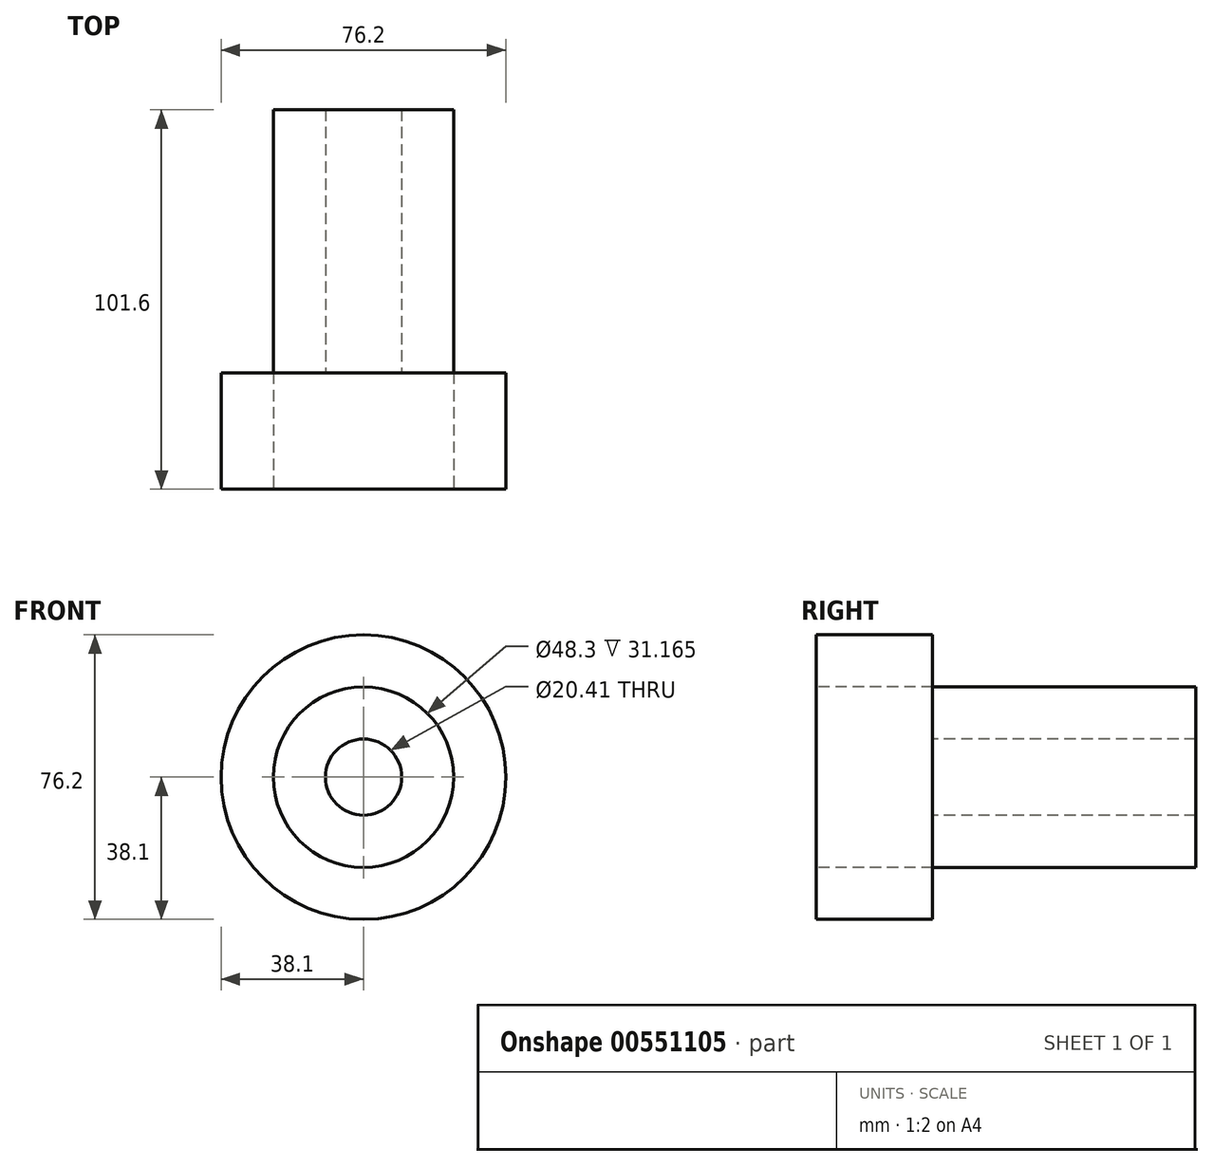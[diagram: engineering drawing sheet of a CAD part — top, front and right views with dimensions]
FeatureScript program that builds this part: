
annotation { "Feature Type Name" : "Feature", "Feature Type Description" : "" }
export const myFeature = defineFeature(function(context is Context, id is Id, definition is map)
    precondition{}
    {
        {
            var Q0;
            Q0=qCreatedBy(makeId("Right.planeOp"),FACE);
            var sketch = newSketch(context, id + "F0", { "sketchPlane" : qUnion([Q0])});
            skLineSegment(sketch, "E0", {"start": v(-31.17, 0) * mm, "end": v(70.43, 0) * mm, "construction": true});
            skLineSegment(sketch, "E1.bottom", {"start": v(-31.17, 38.1) * mm, "end": v(0, 38.1) * mm});
            skLineSegment(sketch, "E1.top", {"start": v(-31.17, 10.2) * mm, "end": v(0, 10.2) * mm});
            skLineSegment(sketch, "E1.left", {"start": v(-31.17, 38.1) * mm, "end": v(-31.17, 10.2) * mm});
            skLineSegment(sketch, "E1.right", {"start": v(0, 38.1) * mm, "end": v(0, 10.2) * mm});
            skLineSegment(sketch, "E2.bottom", {"start": v(-31.17, 24.15) * mm, "end": v(70.43, 24.15) * mm});
            skLineSegment(sketch, "E2.top", {"start": v(-31.17, 10.2) * mm, "end": v(70.43, 10.2) * mm});
            skLineSegment(sketch, "E2.left", {"start": v(-31.17, 24.15) * mm, "end": v(-31.17, 10.2) * mm});
            skLineSegment(sketch, "E2.right", {"start": v(70.43, 24.15) * mm, "end": v(70.43, 10.2) * mm});
            skLineSegment(sketch, "E3.MirrorCS", {"start": v(-31.17, -10.2) * mm, "end": v(0, -10.2) * mm});
            skLineSegment(sketch, "E4.MirrorCS", {"start": v(70.43, -24.15) * mm, "end": v(70.43, -10.2) * mm});
            skLineSegment(sketch, "E5.MirrorCS", {"start": v(-31.17, -24.15) * mm, "end": v(-31.17, -10.2) * mm});
            skLineSegment(sketch, "E6.MirrorCS", {"start": v(-31.17, -38.1) * mm, "end": v(0, -38.1) * mm});
            skLineSegment(sketch, "E7.MirrorCS", {"start": v(-31.17, -38.1) * mm, "end": v(-31.17, -10.2) * mm});
            skLineSegment(sketch, "E8.MirrorCS", {"start": v(0, -38.1) * mm, "end": v(0, -10.2) * mm});
            skLineSegment(sketch, "E9.MirrorCS", {"start": v(-31.17, -24.15) * mm, "end": v(70.43, -24.15) * mm});
            skLineSegment(sketch, "E10.MirrorCS", {"start": v(-31.17, -10.2) * mm, "end": v(70.43, -10.2) * mm});
            skSolve(sketch);
        }
        {
            var Q0;
            {var subQ0=sQuery(id+"F0.wireOp",EDGE,"E1.bottom");Q0=makeQuery(id+"F0.imprint","IMPRINT",FACE,{"disambiguationData":[TD([[makeQuery(id+"F0.imprint","IMPRINT",EDGE,{"derivedFrom":subQ0}),-1.0]])]});}
            var Q1;
            {var subQ5=sQuery(id+"F0.wireOp",EDGE,"E2.left");Q1=makeQuery(id+"F0.imprint","IMPRINT",FACE,{"disambiguationData":[TD([[makeQuery(id+"F0.imprint","IMPRINT",EDGE,{"derivedFrom":subQ5}),1.0]])]});}
            var Q2;
            {var subQ5=sQuery(id+"F0.wireOp",EDGE,"E2.right");Q2=makeQuery(id+"F0.imprint","IMPRINT",FACE,{"disambiguationData":[TD([[makeQuery(id+"F0.imprint","IMPRINT",EDGE,{"derivedFrom":subQ5}),-1.0]])]});}
            var Q3;
            Q3=sQuery(id+"F0.wireOp",EDGE,"E0");
            revolve(context, id + "F1", {"entities" : qUnion([Q0, Q1, Q2]), "axis" : qUnion([Q3]), "revolveType" : RevolveType.FULL});
        }
    });
